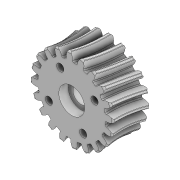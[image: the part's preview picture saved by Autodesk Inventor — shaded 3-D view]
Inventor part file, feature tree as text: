
AUTODESK INVENTOR PART (.ipt)
format: ipt  version: 2022 (Build 260153000, 153)  size: 1,388,544 bytes
history: native  units: in
note: dims shown in document units (in); Inventor stores cm internally (conversion verified against a paired STEP export)
features: extrude x5, sketch x5, pattern_circular x1, projected_geometry x1, other x1
ambient origin geometry x8: Origin, YZ Plane, XZ Plane, XY Plane, X Axis, Y Axis, Z Axis, Center Point
bodies: Solid1 (feature_tree)
feature tree (13):
  extrude  "Extrusion1"  Depth=0.0787in
  extrude  "Extrusion2"  Depth=3.937in TaperAngle=0.0deg
  pattern_circular  "Circular Pattern1"  Count=4 Angle=360.0deg
  extrude  "Extrusion4"  Depth=0.3937in TaperAngle=0.0deg
  extrude  "Extrusion5"  Depth=0.1024in TaperAngle=0.0deg
  extrude  "Extrusion6"  Depth=0.1024in TaperAngle=0.0deg
  sketch  "Sketch1"  dims[d0=3.937in d1=0.0in d2=0.0787in]
  projected_geometry  "Projected Loop1"
  sketch  "Sketch2"  dims[d3=0.2756in d4=3.937in d5=0.0in d6=1.5748in d7=360.0deg]
  sketch  "Sketch4"  dims[d13=0.1772in d14=0.3937in d15=0.0in]
  sketch  "Sketch5"  dims[d17=0.2795in d18=0.1024in d19=0.0in]
  sketch  "Sketch6"  dims[d20=0.2795in d21=0.1024in d22=0.0in]
  other  "Boss-Extrude1"
